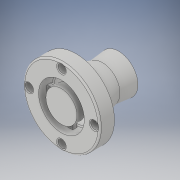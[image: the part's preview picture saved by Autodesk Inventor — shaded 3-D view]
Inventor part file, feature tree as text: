
AUTODESK INVENTOR PART (.ipt)
format: ipt  version: 2019 (Build 230136000, 136)  size: 281,600 bytes
history: native  units: mm
features: fillet x4, sketch x3, extrude x2, revolve x1
ambient origin geometry x8: Origin, YZ Plane, XZ Plane, XY Plane, X Axis, Y Axis, Z Axis, Center Point
bodies: Solid1 (feature_tree)
feature tree (10):
  extrude  "Extrusion1"  Depth=28.0mm
  extrude  "Extrusion2"  Depth=5.0mm
  revolve  "Revolution1"  [1 undecoded]
  fillet  "Fillet1"  Radius=47.0mm
  fillet  "Fillet2"  Radius=5.0mm
  fillet  "Fillet3"  Radius=4.0mm
  fillet  "Fillet5"  Radius=20.0mm
  sketch  "Sketch1"  dims[d0=19.0mm d1=28.0mm]
  sketch  "Sketch2"  dims[d2=5.0mm d3=5.0mm]
  sketch  "Sketch3"  dims[d4=5.0mm d5=5.0mm d7=47.0mm d8=5.0mm d9=0.0mm d10=4.0mm d11=0.0mm d12=20.0mm d21=90.0deg d23=1.0mm d24=28.0mm d25=4.0mm d26=47.0mm d27=0.5mm d28=1.0mm d29=16.580628mm d30=10.0mm d31=1.0mm d33=2.0mm]
note: 1 required parameter value undecoded (feature->parameter linkage not recoverable at this tier; creation-order binding heuristic only, values carry confidence <= 0.55)
